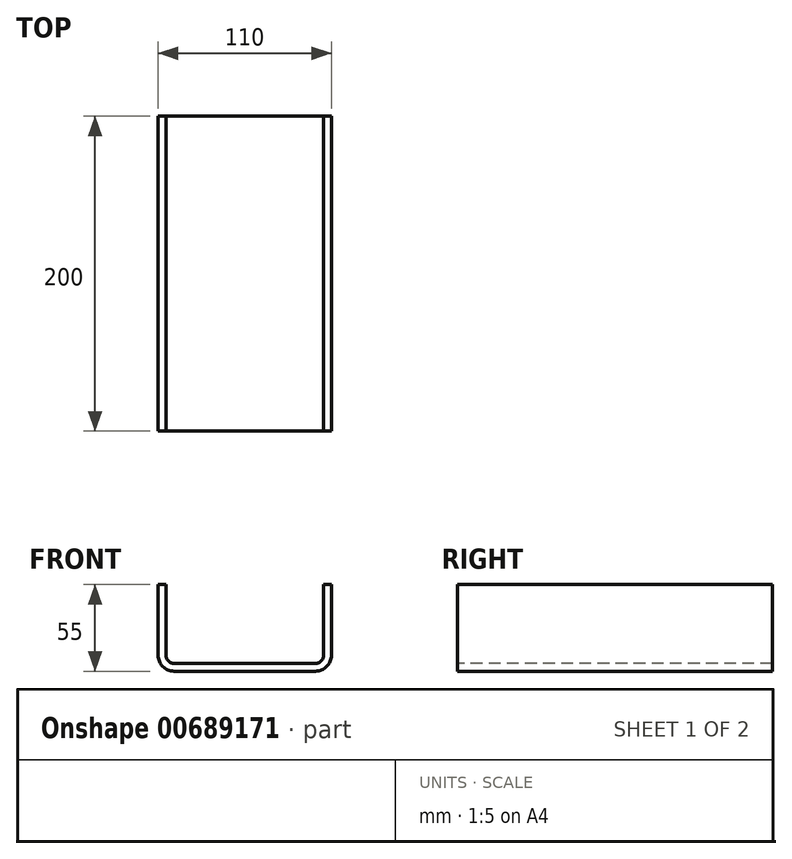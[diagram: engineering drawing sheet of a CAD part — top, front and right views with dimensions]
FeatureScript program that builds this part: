
annotation { "Feature Type Name" : "Feature", "Feature Type Description" : "" }
export const myFeature = defineFeature(function(context is Context, id is Id, definition is map)
    precondition{}
    {
        {
            var Q0;
            Q0=qCreatedBy(makeId("Front.planeOp"),FACE);
            var sketch = newSketch(context, id + "F0", { "sketchPlane" : qUnion([Q0])});
            skLineSegment(sketch, "E0", {"start": v(0, 0) * mm, "end": v(100, 0) * mm});
            skLineSegment(sketch, "E1", {"start": v(100, 0) * mm, "end": v(100, 50) * mm});
            skLineSegment(sketch, "E2", {"start": v(0, 0) * mm, "end": v(0, 50) * mm});
            skLineSegment(sketch, "E3.0", {"start": v(105, -5) * mm, "end": v(105, 50) * mm});
            skLineSegment(sketch, "E3.1", {"start": v(-5, -5) * mm, "end": v(105, -5) * mm});
            skLineSegment(sketch, "E3.2", {"start": v(-5, -5) * mm, "end": v(-5, 50) * mm});
            skLineSegment(sketch, "E4", {"start": v(105, 50) * mm, "end": v(100, 50) * mm});
            skLineSegment(sketch, "E5", {"start": v(0, 50) * mm, "end": v(-5, 50) * mm});
            skSolve(sketch);
        }
        {
            var Q0;
            Q0=makeQuery(id+"F0.imprint","IMPRINT",FACE,{"disambiguationData":[TD([[makeQuery(id+"F0.imprint","IMPRINT",EDGE,{"derivedFrom":sQuery(id+"F0.wireOp",EDGE,"E0")}),-1.0]])]});
            extrude(context, id + "F1", {"entities" : qUnion([Q0]), "oppositeDirection" : true, "depth" : 200 * mm, "offsetDistance" : 25 * mm});
        }
        {
            var Q0;
            Q0=makeQuery(id+"F1.opExtrude","SWEPT_EDGE",EDGE,{"disambiguationData":[OSD([sQuery(id+"F0.wireOp",EDGE,"E0"),sQuery(id+"F0.wireOp",EDGE,"E2")])]});
            var Q1;
            Q1=makeQuery(id+"F1.opExtrude","SWEPT_EDGE",EDGE,{"disambiguationData":[OSD([sQuery(id+"F0.wireOp",EDGE,"E0"),sQuery(id+"F0.wireOp",EDGE,"E1")])]});
            fillet(context, id + "F2", {"entities" : qUnion([Q0, Q1]), "radius" : 5 * mm, "tangentPropagation" : true, "allowEdgeOverflow" : false});
        }
        {
            var Q0;
            Q0=makeQuery(id+"F1.opExtrude","SWEPT_EDGE",EDGE,{"disambiguationData":[OSD([sQuery(id+"F0.wireOp",EDGE,"E3.0"),sQuery(id+"F0.wireOp",EDGE,"E3.1")])]});
            var Q1;
            Q1=makeQuery(id+"F1.opExtrude","SWEPT_EDGE",EDGE,{"disambiguationData":[OSD([sQuery(id+"F0.wireOp",EDGE,"E3.1"),sQuery(id+"F0.wireOp",EDGE,"E3.2")])]});
            fillet(context, id + "F3", {"entities" : qUnion([Q0, Q1]), "radius" : 10 * mm, "tangentPropagation" : true, "allowEdgeOverflow" : false});
        }
    });
